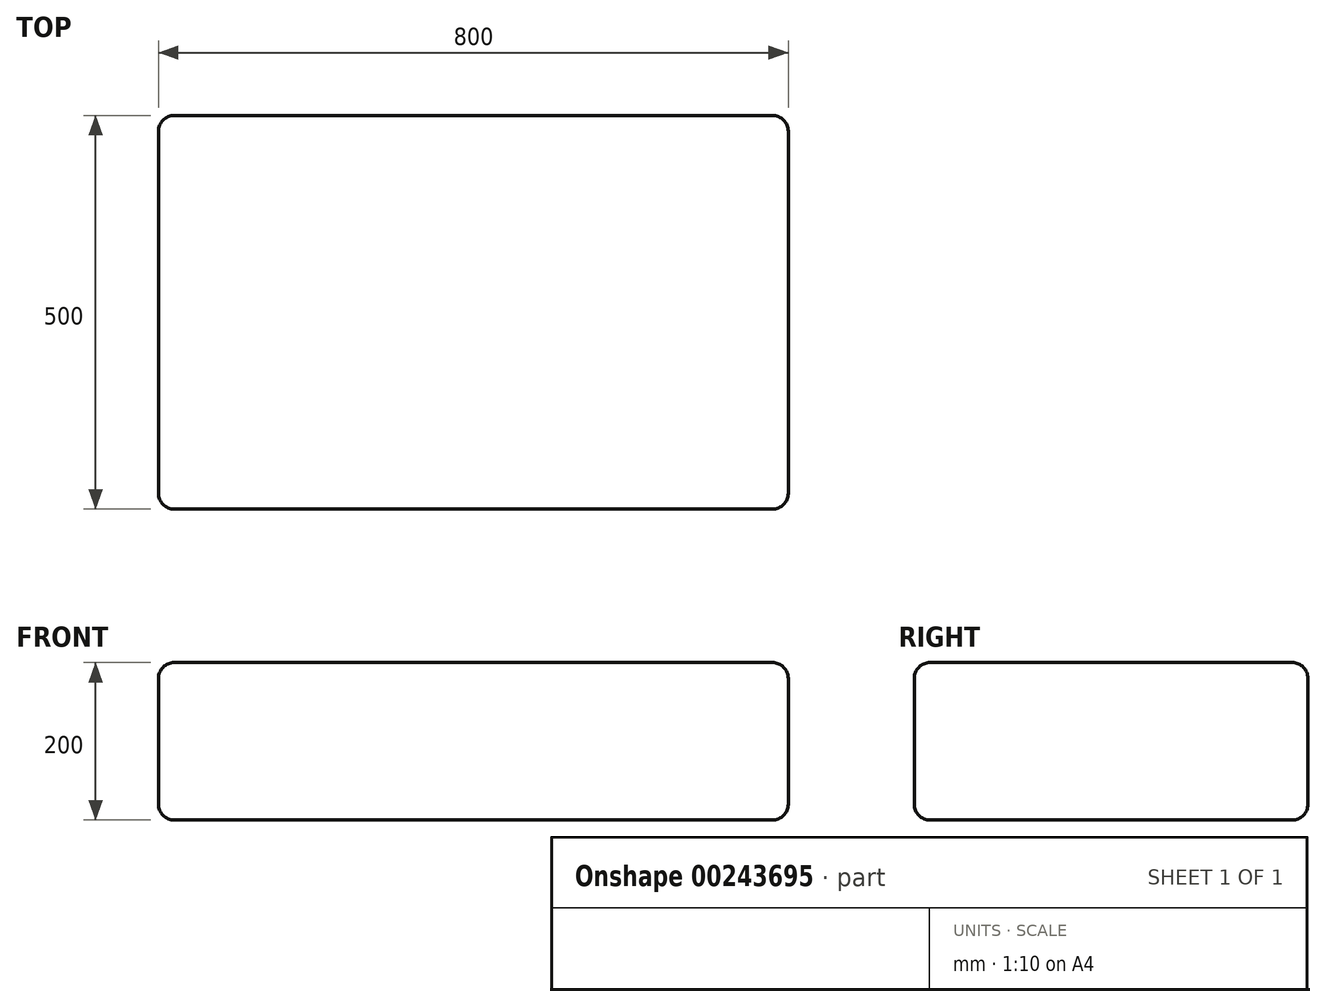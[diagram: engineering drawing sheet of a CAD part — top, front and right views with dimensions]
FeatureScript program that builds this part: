
annotation { "Feature Type Name" : "Feature", "Feature Type Description" : "" }
export const myFeature = defineFeature(function(context is Context, id is Id, definition is map)
    precondition{}
    {
        {
            var Q0;
            Q0=qCreatedBy(makeId("Top.planeOp"),FACE);
            var sketch = newSketch(context, id + "F0", { "sketchPlane" : qUnion([Q0])});
            skLineSegment(sketch, "E0.bottom", {"start": v(-400, 250) * mm, "end": v(400, 250) * mm});
            skLineSegment(sketch, "E0.top", {"start": v(-400, -250) * mm, "end": v(400, -250) * mm});
            skLineSegment(sketch, "E0.left", {"start": v(-400, 250) * mm, "end": v(-400, -250) * mm});
            skLineSegment(sketch, "E0.right", {"start": v(400, 250) * mm, "end": v(400, -250) * mm});
            skLineSegment(sketch, "E1", {"start": v(0, 250) * mm, "end": v(0, -250) * mm, "construction": true});
            skLineSegment(sketch, "E2", {"start": v(-400, 0) * mm, "end": v(400, 0) * mm, "construction": true});
            skSolve(sketch);
        }
        {
            var Q0;
            Q0=makeQuery(id+"F0.imprint","IMPRINT",FACE,{"disambiguationData":[TD([[makeQuery(id+"F0.imprint","IMPRINT",EDGE,{"derivedFrom":sQuery(id+"F0.wireOp",EDGE,"E0.bottom")}),-1.0]])]});
            extrude(context, id + "F1", {"entities" : qUnion([Q0]), "endBound" : BoundingType.SYMMETRIC, "depth" : 200 * mm});
        }
        {
            var Q0;
            Q0=makeQuery(id+"F1.opExtrude","SWEPT_EDGE",EDGE,{"disambiguationData":[OSD([sQuery(id+"F0.wireOp",EDGE,"E0.top"),sQuery(id+"F0.wireOp",EDGE,"E0.left")])]});
            var Q1;
            Q1=makeQuery(id+"F1.opExtrude","SWEPT_EDGE",EDGE,{"disambiguationData":[OSD([sQuery(id+"F0.wireOp",EDGE,"E0.top"),sQuery(id+"F0.wireOp",EDGE,"E0.right")])]});
            var Q2;
            Q2=makeQuery(id+"F1.opExtrude","SWEPT_EDGE",EDGE,{"disambiguationData":[OSD([sQuery(id+"F0.wireOp",EDGE,"E0.bottom"),sQuery(id+"F0.wireOp",EDGE,"E0.right")])]});
            var Q3;
            Q3=makeQuery(id+"F1.opExtrude","SWEPT_EDGE",EDGE,{"disambiguationData":[OSD([sQuery(id+"F0.wireOp",EDGE,"E0.bottom"),sQuery(id+"F0.wireOp",EDGE,"E0.left")])]});
            var Q4;
            Q4=makeQuery(id+"F1.opExtrude","CAP_EDGE",EDGE,{"disambiguationData":[OSD([sQuery(id+"F0.wireOp",EDGE,"E0.top")])],"isStart":false});
            var Q5;
            Q5=makeQuery(id+"F1.opExtrude","CAP_EDGE",EDGE,{"disambiguationData":[OSD([sQuery(id+"F0.wireOp",EDGE,"E0.left")])],"isStart":false});
            var Q6;
            Q6=makeQuery(id+"F1.opExtrude","CAP_EDGE",EDGE,{"disambiguationData":[OSD([sQuery(id+"F0.wireOp",EDGE,"E0.bottom")])],"isStart":false});
            var Q7;
            Q7=makeQuery(id+"F1.opExtrude","CAP_EDGE",EDGE,{"disambiguationData":[OSD([sQuery(id+"F0.wireOp",EDGE,"E0.right")])],"isStart":false});
            var Q8;
            Q8=makeQuery(id+"F1.opExtrude","CAP_EDGE",EDGE,{"disambiguationData":[OSD([sQuery(id+"F0.wireOp",EDGE,"E0.right")])],"isStart":true});
            var Q9;
            Q9=makeQuery(id+"F1.opExtrude","CAP_EDGE",EDGE,{"disambiguationData":[OSD([sQuery(id+"F0.wireOp",EDGE,"E0.top")])],"isStart":true});
            var Q10;
            Q10=makeQuery(id+"F1.opExtrude","CAP_EDGE",EDGE,{"disambiguationData":[OSD([sQuery(id+"F0.wireOp",EDGE,"E0.bottom")])],"isStart":true});
            var Q11;
            Q11=makeQuery(id+"F1.opExtrude","CAP_EDGE",EDGE,{"disambiguationData":[OSD([sQuery(id+"F0.wireOp",EDGE,"E0.left")])],"isStart":true});
            fillet(context, id + "F2", {"entities" : qUnion([Q0, Q1, Q2, Q3, Q4, Q5, Q6, Q7, Q8, Q9, Q10, Q11]), "radius" : 20 * mm, "tangentPropagation" : true, "allowEdgeOverflow" : false});
        }
    });
